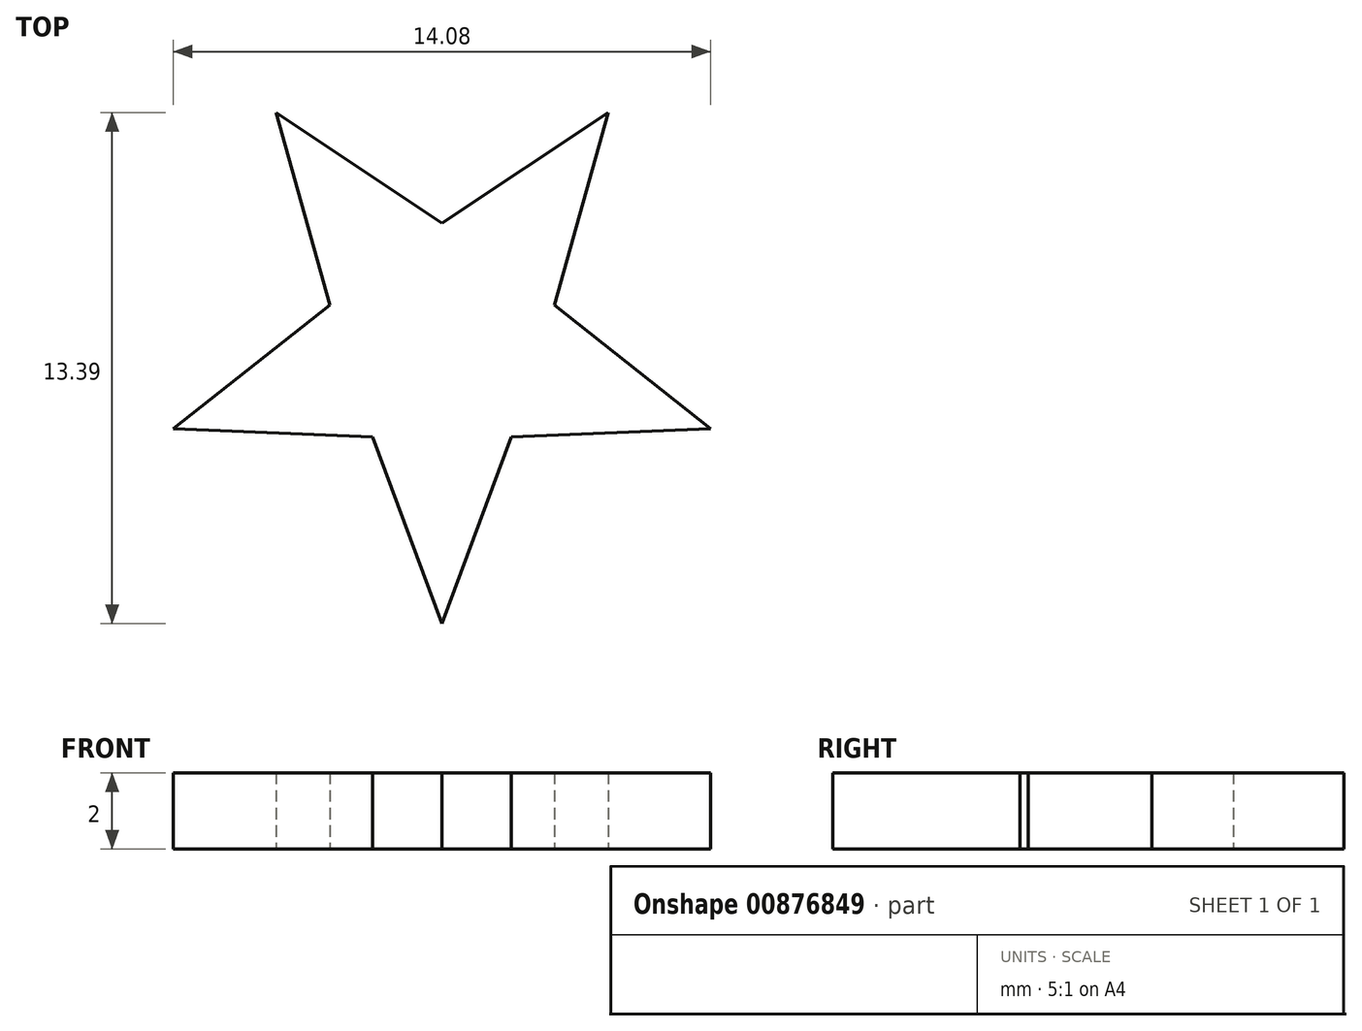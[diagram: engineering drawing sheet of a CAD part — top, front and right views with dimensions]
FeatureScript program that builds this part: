
annotation { "Feature Type Name" : "Feature", "Feature Type Description" : "" }
export const myFeature = defineFeature(function(context is Context, id is Id, definition is map)
    precondition{}
    {
        {
            var Q0;
            Q0=qCreatedBy(makeId("Top.planeOp"),FACE);
            var sketch = newSketch(context, id + "F0", { "sketchPlane" : qUnion([Q0])});
            skCircle(sketch, "E0.cCircle", {"center": v(0, 0) * mm, "radius": 2.5 * mm, "construction": true});
            skLineSegment(sketch, "E0.0", {"start": v(0, 3.1) * mm, "end": v(2.94, 0.95) * mm});
            skLineSegment(sketch, "E0.1", {"start": v(2.94, 0.95) * mm, "end": v(1.82, -2.5) * mm});
            skLineSegment(sketch, "E0.2", {"start": v(1.82, -2.5) * mm, "end": v(-1.82, -2.5) * mm});
            skLineSegment(sketch, "E0.3", {"start": v(-1.82, -2.5) * mm, "end": v(-2.94, 0.95) * mm});
            skLineSegment(sketch, "E0.4", {"start": v(-2.94, 0.95) * mm, "end": v(0, 3.1) * mm});
            skPoint(sketch, "E0.0.midPoint", {"position": v(1.47, 2.02) * mm});
            skLineSegment(sketch, "E1", {"start": v(0, -2.5) * mm, "end": v(0, -7.4) * mm});
            skLineSegment(sketch, "E2", {"start": v(1.82, -2.5) * mm, "end": v(0, -7.4) * mm});
            skLineSegment(sketch, "E3", {"start": v(-1.82, -2.5) * mm, "end": v(0, -7.4) * mm});
            skLineSegment(sketch, "E4.1.0", {"start": v(2.94, 0.95) * mm, "end": v(7.04, -2.29) * mm});
            skLineSegment(sketch, "E4.1.1", {"start": v(1.82, -2.5) * mm, "end": v(7.04, -2.29) * mm});
            skLineSegment(sketch, "E4.2.0", {"start": v(0, 3.1) * mm, "end": v(4.35, 5.99) * mm});
            skLineSegment(sketch, "E4.2.1", {"start": v(2.94, 0.95) * mm, "end": v(4.35, 5.99) * mm});
            skLineSegment(sketch, "E4.3.0", {"start": v(-2.94, 0.95) * mm, "end": v(-4.35, 5.99) * mm});
            skLineSegment(sketch, "E4.3.1", {"start": v(0, 3.1) * mm, "end": v(-4.35, 5.99) * mm});
            skLineSegment(sketch, "E4.4.0", {"start": v(-1.82, -2.5) * mm, "end": v(-7.04, -2.29) * mm});
            skLineSegment(sketch, "E4.4.1", {"start": v(-2.94, 0.95) * mm, "end": v(-7.04, -2.29) * mm});
            skSolve(sketch);
        }
        {
            var Q0;
            Q0=makeQuery(id+"F0.imprint","IMPRINT",FACE,{"disambiguationData":[TD([[makeQuery(id+"F0.imprint","IMPRINT",EDGE,{"derivedFrom":sQuery(id+"F0.wireOp",EDGE,"E0.4")}),1.0]])]});
            var Q1;
            Q1=makeQuery(id+"F0.imprint","IMPRINT",FACE,{"disambiguationData":[TD([[makeQuery(id+"F0.imprint","IMPRINT",EDGE,{"derivedFrom":sQuery(id+"F0.wireOp",EDGE,"E0.0")}),1.0]])]});
            var Q2;
            Q2=makeQuery(id+"F0.imprint","IMPRINT",FACE,{"disambiguationData":[TD([[makeQuery(id+"F0.imprint","IMPRINT",EDGE,{"derivedFrom":sQuery(id+"F0.wireOp",EDGE,"E0.0")}),-1.0]])]});
            var Q3;
            Q3=makeQuery(id+"F0.imprint","IMPRINT",FACE,{"disambiguationData":[TD([[makeQuery(id+"F0.imprint","IMPRINT",EDGE,{"derivedFrom":sQuery(id+"F0.wireOp",EDGE,"E0.3")}),1.0]])]});
            var Q4;
            {var subQ2=sQuery(id+"F0.wireOp",EDGE,"E1");Q4=makeQuery(id+"F0.imprint","IMPRINT",FACE,{"disambiguationData":[TD([[makeQuery(id+"F0.imprint","IMPRINT",EDGE,{"derivedFrom":subQ2}),-1.0]])]});}
            var Q5;
            Q5=makeQuery(id+"F0.imprint","IMPRINT",FACE,{"disambiguationData":[TD([[makeQuery(id+"F0.imprint","IMPRINT",EDGE,{"derivedFrom":sQuery(id+"F0.wireOp",EDGE,"E0.1")}),1.0]])]});
            var Q6;
            {var subQ2=sQuery(id+"F0.wireOp",EDGE,"E1");Q6=makeQuery(id+"F0.imprint","IMPRINT",FACE,{"disambiguationData":[TD([[makeQuery(id+"F0.imprint","IMPRINT",EDGE,{"derivedFrom":subQ2}),1.0]])]});}
            extrude(context, id + "F1", {"entities" : qUnion([Q0, Q1, Q2, Q3, Q4, Q5, Q6]), "depth" : 2 * mm, "offsetDistance" : 25 * mm});
        }
    });
